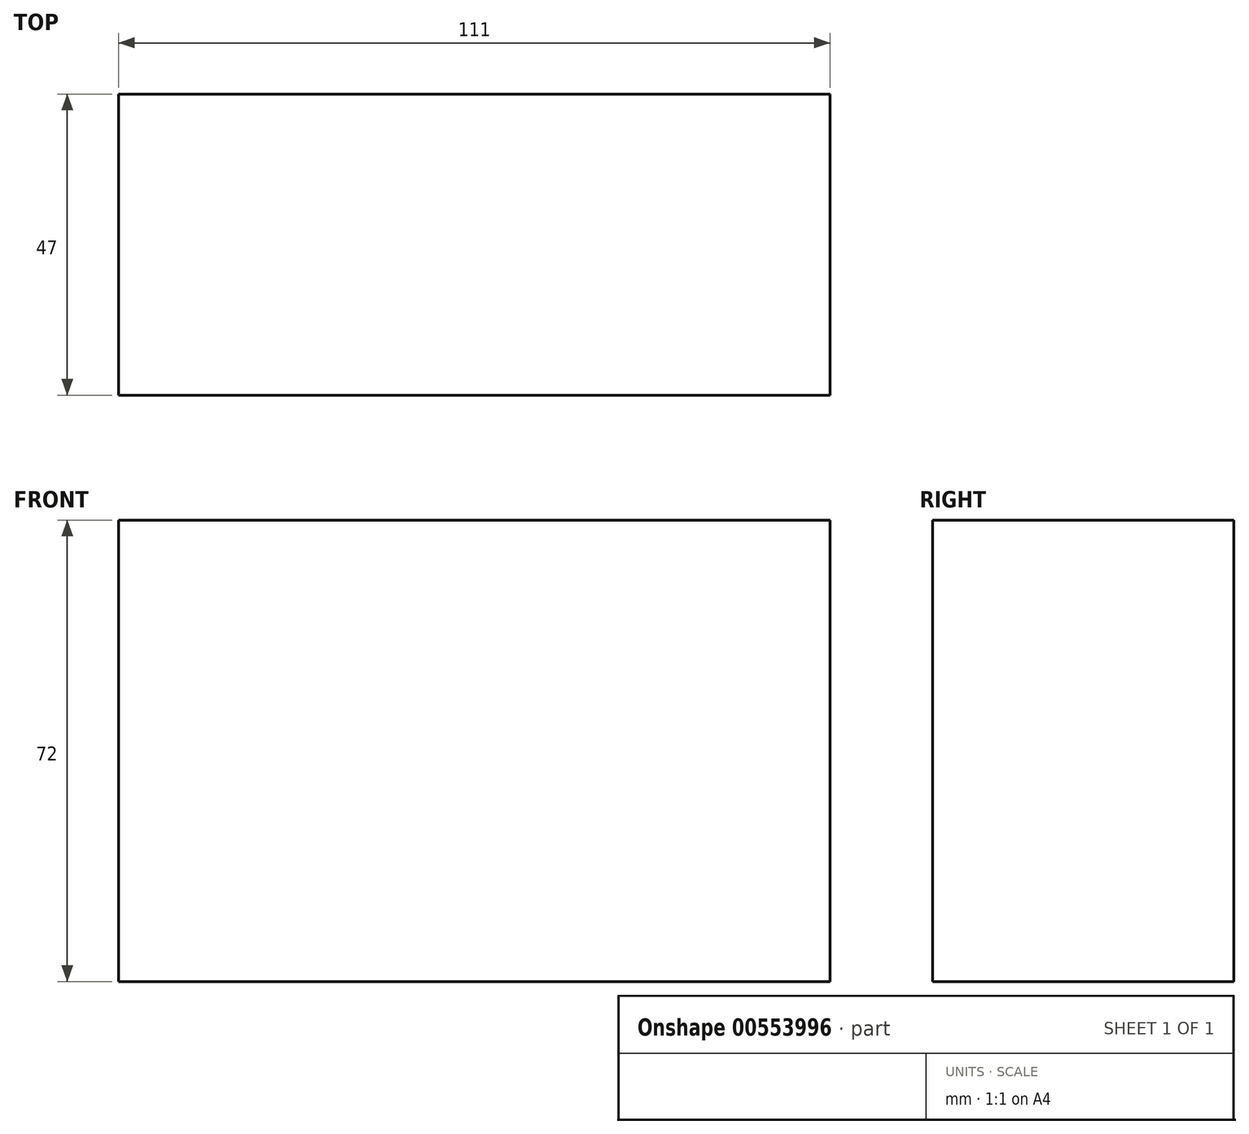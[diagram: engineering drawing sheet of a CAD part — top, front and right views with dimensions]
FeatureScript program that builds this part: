
annotation { "Feature Type Name" : "Feature", "Feature Type Description" : "" }
export const myFeature = defineFeature(function(context is Context, id is Id, definition is map)
    precondition{}
    {
        {
            var Q0;
            Q0=qCreatedBy(makeId("Front.planeOp"),FACE);
            var sketch = newSketch(context, id + "F0", { "sketchPlane" : qUnion([Q0])});
            skLineSegment(sketch, "E0.bottom", {"start": v(55.5, -36) * mm, "end": v(-55.5, -36) * mm});
            skLineSegment(sketch, "E0.top", {"start": v(55.5, 36) * mm, "end": v(-55.5, 36) * mm});
            skLineSegment(sketch, "E0.left", {"start": v(55.5, -36) * mm, "end": v(55.5, 36) * mm});
            skLineSegment(sketch, "E0.right", {"start": v(-55.5, -36) * mm, "end": v(-55.5, 36) * mm});
            skPoint(sketch, "E0.middle", {"position": v(0, 0) * mm});
            skSolve(sketch);
        }
        {
            var Q0;
            Q0=makeQuery(id+"F0.imprint","IMPRINT",FACE,{"disambiguationData":[TD([[makeQuery(id+"F0.imprint","IMPRINT",EDGE,{"derivedFrom":sQuery(id+"F0.wireOp",EDGE,"E0.bottom")}),-1.0]])]});
            extrude(context, id + "F1", {"entities" : qUnion([Q0]), "depth" : 47 * mm, "offsetDistance" : 25 * mm});
        }
    });
